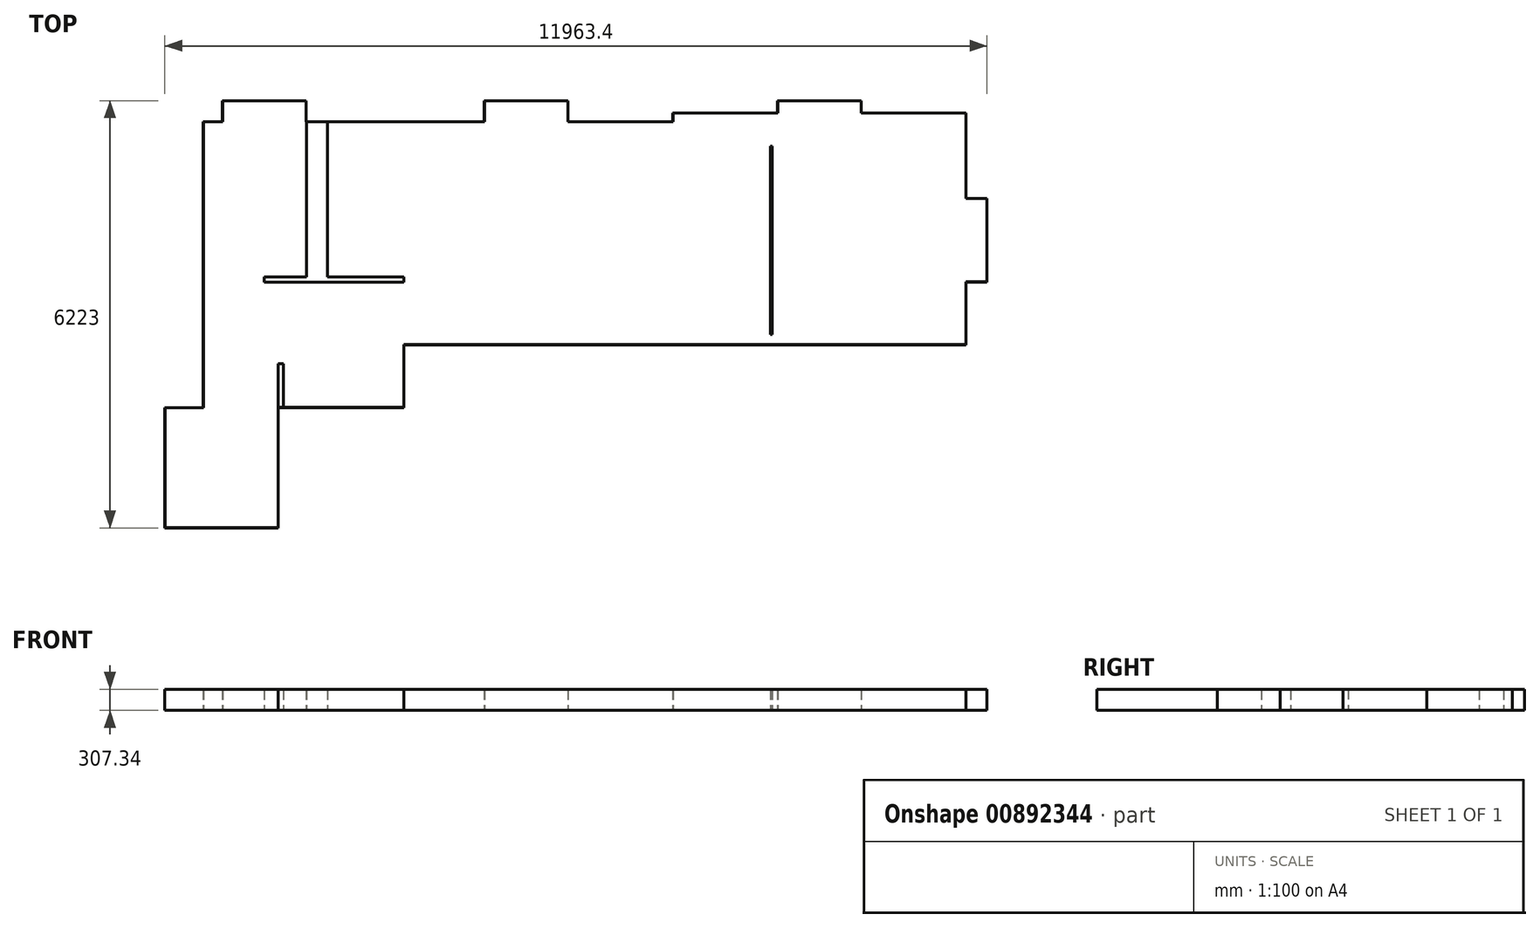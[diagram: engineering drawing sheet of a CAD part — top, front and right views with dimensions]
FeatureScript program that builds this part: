
annotation { "Feature Type Name" : "Feature", "Feature Type Description" : "" }
export const myFeature = defineFeature(function(context is Context, id is Id, definition is map)
    precondition{}
    {
        {
            var Q0;
            Q0=qCreatedBy(makeId("Top.planeOp"),FACE);
            var sketch = newSketch(context, id + "F0", { "sketchPlane" : qUnion([Q0])});
            skLineSegment(sketch, "E0", {"start": v(-2921, -914.4) * mm, "end": v(-2921, 3251.2) * mm});
            skLineSegment(sketch, "E1", {"start": v(-2921, 3251.2) * mm, "end": v(-2641.6, 3251.2) * mm});
            skLineSegment(sketch, "E2", {"start": v(-2641.6, 3251.2) * mm, "end": v(-2641.6, 3556) * mm});
            skLineSegment(sketch, "E3", {"start": v(-2641.6, 3556) * mm, "end": v(-1422.4, 3556) * mm});
            skLineSegment(sketch, "E4", {"start": v(-1422.4, 3556) * mm, "end": v(-1422.4, 3251.2) * mm});
            skLineSegment(sketch, "E5", {"start": v(-1422.4, 3251.2) * mm, "end": v(1168.4, 3251.2) * mm});
            skLineSegment(sketch, "E6", {"start": v(1168.4, 3251.2) * mm, "end": v(1168.4, 3556) * mm});
            skLineSegment(sketch, "E7", {"start": v(1168.4, 3556) * mm, "end": v(2387.6, 3556) * mm});
            skLineSegment(sketch, "E8", {"start": v(2387.6, 3556) * mm, "end": v(2387.6, 3251.2) * mm});
            skLineSegment(sketch, "E9", {"start": v(2387.6, 3251.2) * mm, "end": v(3911.6, 3251.2) * mm});
            skLineSegment(sketch, "E10", {"start": v(3911.6, 3251.2) * mm, "end": v(3911.6, 3378.2) * mm});
            skLineSegment(sketch, "E11", {"start": v(3911.6, 3378.2) * mm, "end": v(5435.6, 3378.2) * mm});
            skLineSegment(sketch, "E12", {"start": v(5435.6, 3378.2) * mm, "end": v(5435.6, 3556) * mm});
            skLineSegment(sketch, "E13", {"start": v(5435.6, 3556) * mm, "end": v(6654.8, 3556) * mm});
            skLineSegment(sketch, "E14", {"start": v(6654.8, 3556) * mm, "end": v(6654.8, 3378.2) * mm});
            skLineSegment(sketch, "E15", {"start": v(6654.8, 3378.2) * mm, "end": v(8178.8, 3378.2) * mm});
            skLineSegment(sketch, "E16", {"start": v(8178.8, 3378.2) * mm, "end": v(8178.8, 2133.6) * mm});
            skLineSegment(sketch, "E17", {"start": v(8178.8, 2133.6) * mm, "end": v(8483.6, 2133.6) * mm});
            skLineSegment(sketch, "E18", {"start": v(8483.6, 2133.6) * mm, "end": v(8483.6, 914.4) * mm});
            skLineSegment(sketch, "E19", {"start": v(8483.6, 914.4) * mm, "end": v(8178.8, 914.4) * mm});
            skLineSegment(sketch, "E20", {"start": v(8178.8, 914.4) * mm, "end": v(8178.8, 0) * mm});
            skLineSegment(sketch, "E21", {"start": v(8178.8, 0) * mm, "end": v(0, 0) * mm});
            skLineSegment(sketch, "E22", {"start": v(0, 0) * mm, "end": v(0, -914.4) * mm});
            skLineSegment(sketch, "E23", {"start": v(0, -914.4) * mm, "end": v(-1828.8, -914.4) * mm});
            skLineSegment(sketch, "E24", {"start": v(-1828.8, -914.4) * mm, "end": v(-1828.8, -2667) * mm});
            skLineSegment(sketch, "E25", {"start": v(-1828.8, -2667) * mm, "end": v(-3479.8, -2667) * mm});
            skLineSegment(sketch, "E26", {"start": v(-3479.8, -2667) * mm, "end": v(-3479.8, -914.4) * mm});
            skLineSegment(sketch, "E27", {"start": v(-3479.8, -914.4) * mm, "end": v(-2921, -914.4) * mm});
            skSolve(sketch);
        }
        {
            var Q0;
            Q0 = qSketchRegion(id + "F0", true);
            extrude(context, id + "F1", {"entities" : qUnion([Q0]), "depth" : 304.8 * mm, "offsetDistance" : 25.4 * mm});
        }
        {
            var Q0;
            Q0=makeQuery(id+"F1.opExtrude","CAP_FACE",FACE,{"disambiguationData":[OSD([sQuery(id+"F0.wireOp",EDGE,"E0"),sQuery(id+"F0.wireOp",EDGE,"E1"),sQuery(id+"F0.wireOp",EDGE,"E2"),sQuery(id+"F0.wireOp",EDGE,"E3"),sQuery(id+"F0.wireOp",EDGE,"E4"),sQuery(id+"F0.wireOp",EDGE,"E5"),sQuery(id+"F0.wireOp",EDGE,"E6"),sQuery(id+"F0.wireOp",EDGE,"E7"),sQuery(id+"F0.wireOp",EDGE,"E8"),sQuery(id+"F0.wireOp",EDGE,"E9"),sQuery(id+"F0.wireOp",EDGE,"E10"),sQuery(id+"F0.wireOp",EDGE,"E11"),sQuery(id+"F0.wireOp",EDGE,"E12"),sQuery(id+"F0.wireOp",EDGE,"E13"),sQuery(id+"F0.wireOp",EDGE,"E14"),sQuery(id+"F0.wireOp",EDGE,"E15"),sQuery(id+"F0.wireOp",EDGE,"E16"),sQuery(id+"F0.wireOp",EDGE,"E17"),sQuery(id+"F0.wireOp",EDGE,"E18"),sQuery(id+"F0.wireOp",EDGE,"E19"),sQuery(id+"F0.wireOp",EDGE,"E20"),sQuery(id+"F0.wireOp",EDGE,"E21"),sQuery(id+"F0.wireOp",EDGE,"E22"),sQuery(id+"F0.wireOp",EDGE,"E23"),sQuery(id+"F0.wireOp",EDGE,"E24"),sQuery(id+"F0.wireOp",EDGE,"E25"),sQuery(id+"F0.wireOp",EDGE,"E26"),sQuery(id+"F0.wireOp",EDGE,"E27")])],"isStart":false});
            shell(context, id + "F2", {"entities" : qUnion([Q0]), "thickness" : 2.54 * mm});
        }
        {
            var Q0;
            Q0=makeQuery(id+"F2.opShell","OFFSET_FACE",FACE,{"disambiguationData":[OSD([sQuery(id+"F0.wireOp",EDGE,"E0"),sQuery(id+"F0.wireOp",EDGE,"E1"),sQuery(id+"F0.wireOp",EDGE,"E2"),sQuery(id+"F0.wireOp",EDGE,"E3"),sQuery(id+"F0.wireOp",EDGE,"E4"),sQuery(id+"F0.wireOp",EDGE,"E5"),sQuery(id+"F0.wireOp",EDGE,"E6"),sQuery(id+"F0.wireOp",EDGE,"E7"),sQuery(id+"F0.wireOp",EDGE,"E8"),sQuery(id+"F0.wireOp",EDGE,"E9"),sQuery(id+"F0.wireOp",EDGE,"E10"),sQuery(id+"F0.wireOp",EDGE,"E11"),sQuery(id+"F0.wireOp",EDGE,"E12"),sQuery(id+"F0.wireOp",EDGE,"E13"),sQuery(id+"F0.wireOp",EDGE,"E14"),sQuery(id+"F0.wireOp",EDGE,"E15"),sQuery(id+"F0.wireOp",EDGE,"E16"),sQuery(id+"F0.wireOp",EDGE,"E17"),sQuery(id+"F0.wireOp",EDGE,"E18"),sQuery(id+"F0.wireOp",EDGE,"E19"),sQuery(id+"F0.wireOp",EDGE,"E20"),sQuery(id+"F0.wireOp",EDGE,"E21"),sQuery(id+"F0.wireOp",EDGE,"E22"),sQuery(id+"F0.wireOp",EDGE,"E23"),sQuery(id+"F0.wireOp",EDGE,"E24"),sQuery(id+"F0.wireOp",EDGE,"E25"),sQuery(id+"F0.wireOp",EDGE,"E26"),sQuery(id+"F0.wireOp",EDGE,"E27")])]});
            var sketch = newSketch(context, id + "F3", { "sketchPlane" : qUnion([Q0])});
            skLineSegment(sketch, "E28", {"start": v(-1419.86, 3248.66) * mm, "end": v(-1419.86, 988.06) * mm});
            skLineSegment(sketch, "E29", {"start": v(-1419.86, 988.06) * mm, "end": v(-2032, 988.06) * mm});
            skLineSegment(sketch, "E30", {"start": v(-2032, 988.06) * mm, "end": v(-2032, 911.86) * mm});
            skLineSegment(sketch, "E31", {"start": v(-2032, 911.86) * mm, "end": v(0, 911.86) * mm});
            skLineSegment(sketch, "E32", {"start": v(0, 911.86) * mm, "end": v(0, 988.06) * mm});
            skLineSegment(sketch, "E33", {"start": v(0, 988.06) * mm, "end": v(-1115.06, 988.06) * mm});
            skLineSegment(sketch, "E34", {"start": v(-1115.06, 988.06) * mm, "end": v(-1115.06, 3248.66) * mm});
            skLineSegment(sketch, "E35", {"start": v(-1115.06, 3248.66) * mm, "end": v(-1419.86, 3248.66) * mm});
            skSolve(sketch);
        }
        {
            var Q0;
            Q0 = qSketchRegion(id + "F3", true);
            extrude(context, id + "F4", {"entities" : qUnion([Q0]), "operationType" : NewBodyOperationType.ADD, "depth" : 304.8 * mm, "offsetDistance" : 25.4 * mm});
        }
        {
            var Q0;
            Q0=makeQuery(id+"F2.opShell","OFFSET_FACE",FACE,{"disambiguationData":[OSD([sQuery(id+"F0.wireOp",EDGE,"E0"),sQuery(id+"F0.wireOp",EDGE,"E1"),sQuery(id+"F0.wireOp",EDGE,"E2"),sQuery(id+"F0.wireOp",EDGE,"E3"),sQuery(id+"F0.wireOp",EDGE,"E4"),sQuery(id+"F0.wireOp",EDGE,"E5"),sQuery(id+"F0.wireOp",EDGE,"E6"),sQuery(id+"F0.wireOp",EDGE,"E7"),sQuery(id+"F0.wireOp",EDGE,"E8"),sQuery(id+"F0.wireOp",EDGE,"E9"),sQuery(id+"F0.wireOp",EDGE,"E10"),sQuery(id+"F0.wireOp",EDGE,"E11"),sQuery(id+"F0.wireOp",EDGE,"E12"),sQuery(id+"F0.wireOp",EDGE,"E13"),sQuery(id+"F0.wireOp",EDGE,"E14"),sQuery(id+"F0.wireOp",EDGE,"E15"),sQuery(id+"F0.wireOp",EDGE,"E16"),sQuery(id+"F0.wireOp",EDGE,"E17"),sQuery(id+"F0.wireOp",EDGE,"E18"),sQuery(id+"F0.wireOp",EDGE,"E19"),sQuery(id+"F0.wireOp",EDGE,"E20"),sQuery(id+"F0.wireOp",EDGE,"E21"),sQuery(id+"F0.wireOp",EDGE,"E22"),sQuery(id+"F0.wireOp",EDGE,"E23"),sQuery(id+"F0.wireOp",EDGE,"E24"),sQuery(id+"F0.wireOp",EDGE,"E25"),sQuery(id+"F0.wireOp",EDGE,"E26"),sQuery(id+"F0.wireOp",EDGE,"E27")])]});
            var sketch = newSketch(context, id + "F5", { "sketchPlane" : qUnion([Q0])});
            skLineSegment(sketch, "E36", {"start": v(-1831.34, -911.86) * mm, "end": v(-1831.34, -276.86) * mm});
            skLineSegment(sketch, "E37", {"start": v(-1831.34, -276.86) * mm, "end": v(-1755.14, -276.86) * mm});
            skLineSegment(sketch, "E38", {"start": v(-1755.14, -276.86) * mm, "end": v(-1755.14, -911.86) * mm});
            skLineSegment(sketch, "E39", {"start": v(-1755.14, -911.86) * mm, "end": v(-1831.34, -911.86) * mm});
            skSolve(sketch);
        }
        {
            var Q0;
            Q0 = qSketchRegion(id + "F5", true);
            extrude(context, id + "F6", {"entities" : qUnion([Q0]), "operationType" : NewBodyOperationType.ADD, "depth" : 304.8 * mm, "offsetDistance" : 25.4 * mm});
        }
        {
            var Q0;
            Q0=makeQuery(id+"F2.opShell","OFFSET_FACE",FACE,{"disambiguationData":[OSD([sQuery(id+"F0.wireOp",EDGE,"E0"),sQuery(id+"F0.wireOp",EDGE,"E1"),sQuery(id+"F0.wireOp",EDGE,"E2"),sQuery(id+"F0.wireOp",EDGE,"E3"),sQuery(id+"F0.wireOp",EDGE,"E4"),sQuery(id+"F0.wireOp",EDGE,"E5"),sQuery(id+"F0.wireOp",EDGE,"E6"),sQuery(id+"F0.wireOp",EDGE,"E7"),sQuery(id+"F0.wireOp",EDGE,"E8"),sQuery(id+"F0.wireOp",EDGE,"E9"),sQuery(id+"F0.wireOp",EDGE,"E10"),sQuery(id+"F0.wireOp",EDGE,"E11"),sQuery(id+"F0.wireOp",EDGE,"E12"),sQuery(id+"F0.wireOp",EDGE,"E13"),sQuery(id+"F0.wireOp",EDGE,"E14"),sQuery(id+"F0.wireOp",EDGE,"E15"),sQuery(id+"F0.wireOp",EDGE,"E16"),sQuery(id+"F0.wireOp",EDGE,"E17"),sQuery(id+"F0.wireOp",EDGE,"E18"),sQuery(id+"F0.wireOp",EDGE,"E19"),sQuery(id+"F0.wireOp",EDGE,"E20"),sQuery(id+"F0.wireOp",EDGE,"E21"),sQuery(id+"F0.wireOp",EDGE,"E22"),sQuery(id+"F0.wireOp",EDGE,"E23"),sQuery(id+"F0.wireOp",EDGE,"E24"),sQuery(id+"F0.wireOp",EDGE,"E25"),sQuery(id+"F0.wireOp",EDGE,"E26"),sQuery(id+"F0.wireOp",EDGE,"E27")])]});
            var sketch = newSketch(context, id + "F7", { "sketchPlane" : qUnion([Q0])});
            skLineSegment(sketch, "E40.bottom", {"start": v(5359.4, 152.4) * mm, "end": v(5334, 152.4) * mm});
            skLineSegment(sketch, "E40.top", {"start": v(5359.4, 2895.6) * mm, "end": v(5334, 2895.6) * mm});
            skLineSegment(sketch, "E40.left", {"start": v(5359.4, 152.4) * mm, "end": v(5359.4, 2895.6) * mm});
            skLineSegment(sketch, "E40.right", {"start": v(5334, 152.4) * mm, "end": v(5334, 2895.6) * mm});
            skPoint(sketch, "E40.middle", {"position": v(5346.7, 1524) * mm});
            skSolve(sketch);
        }
        {
            var Q0;
            Q0 = qSketchRegion(id + "F7", true);
            extrude(context, id + "F8", {"entities" : qUnion([Q0]), "operationType" : NewBodyOperationType.ADD, "depth" : 304.8 * mm, "offsetDistance" : 25.4 * mm});
        }
    });
